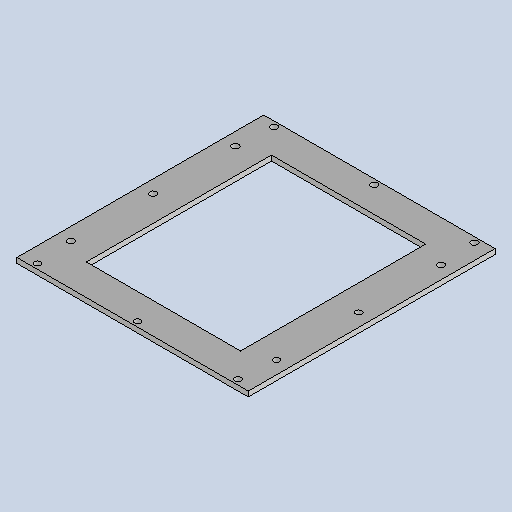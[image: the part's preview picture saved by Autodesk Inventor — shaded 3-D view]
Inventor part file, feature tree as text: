
AUTODESK INVENTOR PART (.ipt)
format: ipt  version: 2025.1 (Build 291241020, 241B)  size: 162,816 bytes
history: native  units: mm
features: other x13, reference x12, sketch x2, sheet_metal_op x1
ambient origin geometry x8: Origin, YZ Plane, XZ Plane, XY Plane, X Axis, Y Axis, Z Axis, Center Point
bodies: Body1 (feature_tree)
feature tree (28):
  sheet_metal_op  "Face2"
  sketch  "Sketch3"  dims[d18=10.0mm]
  other  "Plate3"
  sketch  "Sketch4"  dims[d22=450.0mm d23=480.0mm d24=300.0mm d25=360.0mm d26=10.0mm d27=0.0mm]
  reference  "Reference1"
  reference  "Reference2"
  reference  "Reference3"
  reference  "Reference4"
  reference  "Reference5"
  reference  "Reference6"
  reference  "Reference7"
  reference  "Reference8"
  reference  "Reference9"
  reference  "Reference10"
  reference  "Reference11"
  reference  "Reference12"
  other  "Cut1"
  other  "ASY NDM-VOS_powder_hopper.iam"
  other  "ASY NVPH-400 shredder:1"
  other  "NDM-VOS 112 sredder wall sub:2"
  other  "NDM-VOS 111 sredder wall 1:2"
  other  "ISO 4017 M12 x 40:1"
  other  "ISO 4017 M12 x 40:5"
  other  "ISO 4017 M12 x 40:6"
  other  "ISO 4017 M12 x 40:12"
  other  "ISO 4017 M12 x 40:11"
  other  "NDM-VOS 111 sredder wall 1:1"
  other  "Definition1"
